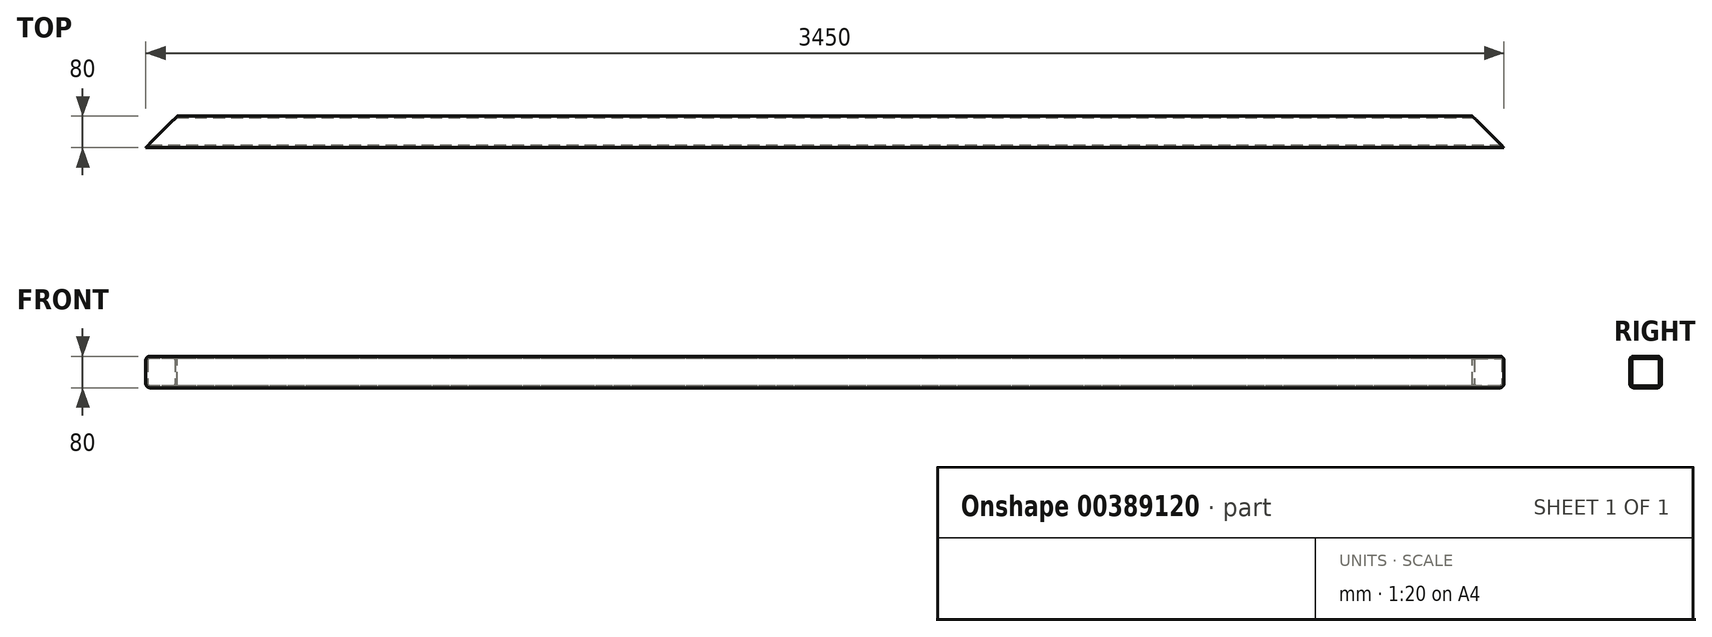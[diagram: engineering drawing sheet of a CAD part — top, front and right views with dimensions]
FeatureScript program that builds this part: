
annotation { "Feature Type Name" : "Feature", "Feature Type Description" : "" }
export const myFeature = defineFeature(function(context is Context, id is Id, definition is map)
    precondition{}
    {
        {
            var Q0;
            Q0=qCreatedBy(makeId("Right.planeOp"),FACE);
            var sketch = newSketch(context, id + "F0", { "sketchPlane" : qUnion([Q0])});
            skLineSegment(sketch, "E0.bottom", {"start": v(30, 40) * mm, "end": v(-30, 40) * mm});
            skLineSegment(sketch, "E0.top", {"start": v(30, -40) * mm, "end": v(-30, -40) * mm});
            skLineSegment(sketch, "E0.left", {"start": v(40, 30) * mm, "end": v(40, -30) * mm});
            skLineSegment(sketch, "E0.right", {"start": v(-40, 30) * mm, "end": v(-40, -30) * mm});
            skPoint(sketch, "E0.middle", {"position": v(0, 0) * mm});
            skPoint(sketch, "E1.visualSharp", {"position": v(-40, 40) * mm});
            skArc(sketch, "E1.filletArc", {"start": v(-30, 40) * mm, "mid": v(-37.07, 37.07) * mm, "end": v(-40, 30) * mm});
            skPoint(sketch, "E2.visualSharp", {"position": v(40, 40) * mm});
            skArc(sketch, "E2.filletArc", {"start": v(40, 30) * mm, "mid": v(37.07, 37.07) * mm, "end": v(30, 40) * mm});
            skPoint(sketch, "E3.visualSharp", {"position": v(40, -40) * mm});
            skArc(sketch, "E3.filletArc", {"start": v(30, -40) * mm, "mid": v(37.07, -37.07) * mm, "end": v(40, -30) * mm});
            skPoint(sketch, "E4.visualSharp", {"position": v(-40, -40) * mm});
            skArc(sketch, "E4.filletArc", {"start": v(-40, -30) * mm, "mid": v(-37.07, -37.07) * mm, "end": v(-30, -40) * mm});
            skArc(sketch, "E5.0", {"start": v(35, 30) * mm, "mid": v(33.54, 33.54) * mm, "end": v(30, 35) * mm});
            skLineSegment(sketch, "E5.1", {"start": v(35, 30) * mm, "end": v(35, -30) * mm});
            skLineSegment(sketch, "E5.2", {"start": v(30, 35) * mm, "end": v(-30, 35) * mm});
            skArc(sketch, "E5.3", {"start": v(30, -35) * mm, "mid": v(33.54, -33.54) * mm, "end": v(35, -30) * mm});
            skArc(sketch, "E5.4", {"start": v(-30, 35) * mm, "mid": v(-33.54, 33.54) * mm, "end": v(-35, 30) * mm});
            skLineSegment(sketch, "E5.5", {"start": v(-35, 30) * mm, "end": v(-35, -30) * mm});
            skArc(sketch, "E5.6", {"start": v(-35, -30) * mm, "mid": v(-33.54, -33.54) * mm, "end": v(-30, -35) * mm});
            skLineSegment(sketch, "E5.7", {"start": v(30, -35) * mm, "end": v(-30, -35) * mm});
            skSolve(sketch);
        }
        {
            var Q0;
            Q0=qSketchRegion(id+"F0",true);
            extrude(context, id + "F1", {"entities" : qUnion([Q0]), "endBound" : BoundingType.SYMMETRIC, "depth" : 3450 * mm});
        }
        {
            var Q0;
            Q0=makeQuery(id+"F1.opExtrude","SWEPT_FACE",FACE,{"disambiguationData":[OSD([sQuery(id+"F0.wireOp",EDGE,"E0.bottom")])]});
            var sketch = newSketch(context, id + "F2", { "sketchPlane" : qUnion([Q0])});
            skLineSegment(sketch, "E6", {"start": v(-1725, -40) * mm, "end": v(-1645, 40) * mm});
            skLineSegment(sketch, "E7", {"start": v(-1645, 40) * mm, "end": v(-1725, 40) * mm});
            skLineSegment(sketch, "E8", {"start": v(-1725, 40) * mm, "end": v(-1725, -40) * mm});
            skLineSegment(sketch, "E9", {"start": v(0, 30) * mm, "end": v(0, -30) * mm, "construction": true});
            skLineSegment(sketch, "E10.MirrorCS", {"start": v(1725, 40) * mm, "end": v(1725, -40) * mm});
            skLineSegment(sketch, "E11.MirrorCS", {"start": v(1725, -40) * mm, "end": v(1645, 40) * mm});
            skLineSegment(sketch, "E12.MirrorCS", {"start": v(1645, 40) * mm, "end": v(1725, 40) * mm});
            skSolve(sketch);
        }
        {
            var Q0;
            Q0 = qSketchRegion(id + "F2", true);
            extrude(context, id + "F3", {"entities" : qUnion([Q0]), "operationType" : NewBodyOperationType.REMOVE, "endBound" : BoundingType.THROUGH_ALL, "oppositeDirection" : true, "depth" : 25 * mm});
        }
    });
